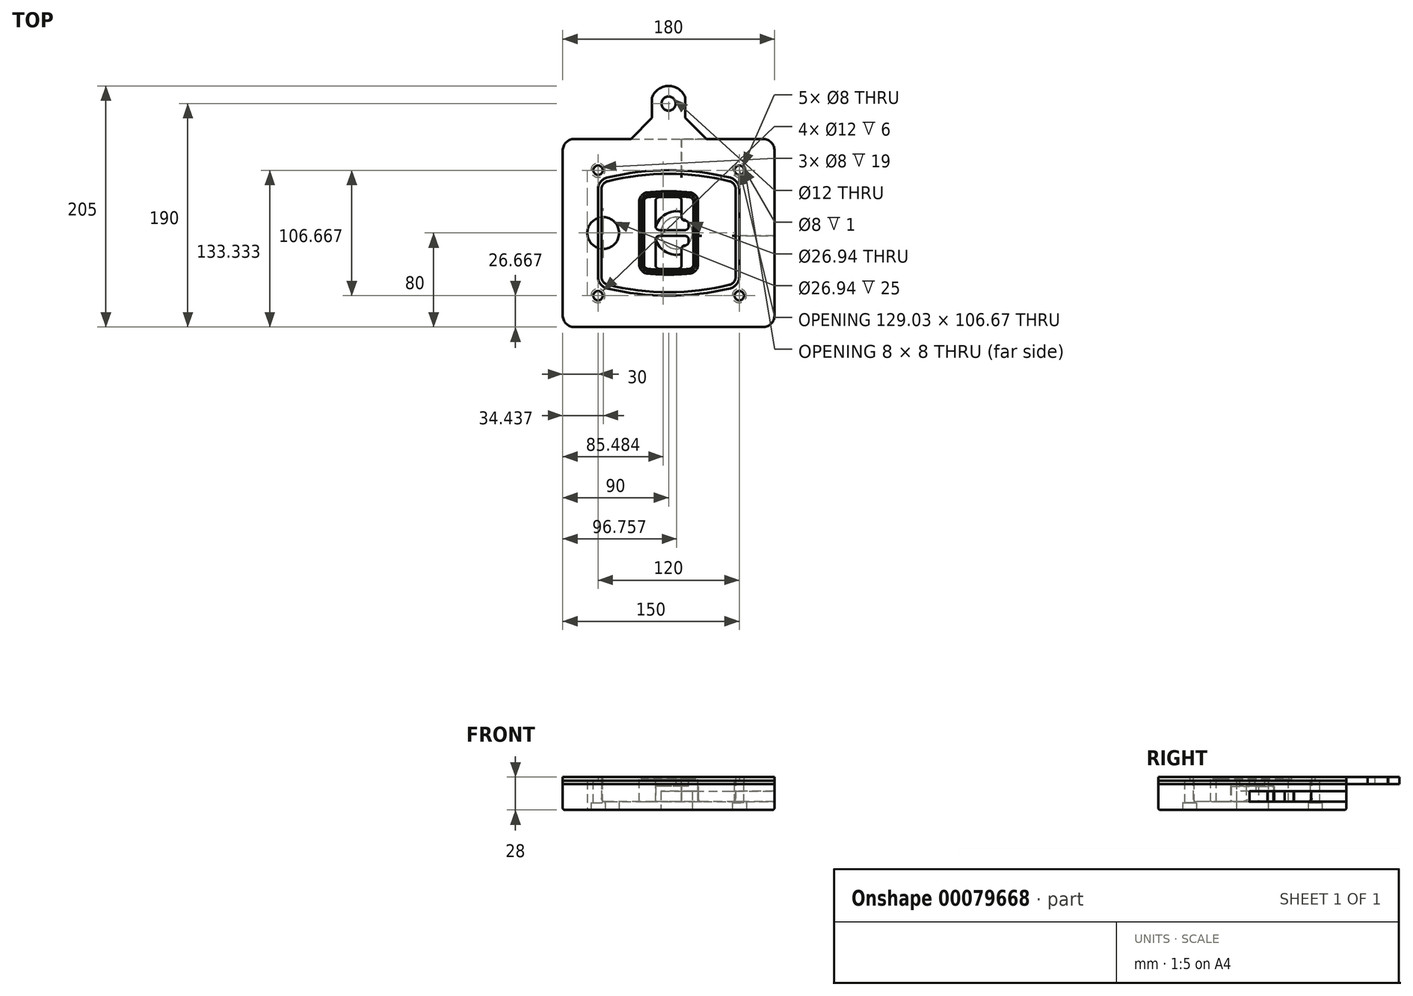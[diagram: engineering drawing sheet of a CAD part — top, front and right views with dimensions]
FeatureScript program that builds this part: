
annotation { "Feature Type Name" : "Feature", "Feature Type Description" : "" }
export const myFeature = defineFeature(function(context is Context, id is Id, definition is map)
    precondition{}
    {
        {
            var Q0;
            Q0=qCreatedBy(makeId("Top.planeOp"),FACE);
            var sketch = newSketch(context, id + "F0", { "sketchPlane" : qUnion([Q0])});
            skPoint(sketch, "E0.rect.middle", {"position": v(0, 0) * mm});
            skLineSegment(sketch, "E1.bottom", {"start": v(-80, -80) * mm, "end": v(80, -80) * mm});
            skLineSegment(sketch, "E1.top", {"start": v(-80, 80) * mm, "end": v(80, 80) * mm});
            skLineSegment(sketch, "E1.left", {"start": v(-90, -70) * mm, "end": v(-90, 70) * mm});
            skLineSegment(sketch, "E1.right", {"start": v(90, -70) * mm, "end": v(90, 70) * mm});
            skLineSegment(sketch, "E2", {"start": v(-90, 80) * mm, "end": v(90, -80) * mm, "construction": true});
            skLineSegment(sketch, "E3", {"start": v(90, 80) * mm, "end": v(-90, -80) * mm, "construction": true});
            skCircle(sketch, "E4", {"center": v(-60, 53.33) * mm, "radius": 4 * mm});
            skCircle(sketch, "E5", {"center": v(60, 53.33) * mm, "radius": 4 * mm});
            skCircle(sketch, "E6", {"center": v(60, -53.33) * mm, "radius": 4 * mm});
            skCircle(sketch, "E7", {"center": v(-60, -53.33) * mm, "radius": 4 * mm});
            skLineSegment(sketch, "E8", {"start": v(-60, 53.33) * mm, "end": v(60, 53.33) * mm, "construction": true});
            skLineSegment(sketch, "E9", {"start": v(60, 53.33) * mm, "end": v(60, -53.33) * mm, "construction": true});
            skLineSegment(sketch, "E10", {"start": v(60, -53.33) * mm, "end": v(-60, -53.33) * mm, "construction": true});
            skLineSegment(sketch, "E11", {"start": v(-60, -53.33) * mm, "end": v(-60, 53.33) * mm, "construction": true});
            skLineSegment(sketch, "E12", {"start": v(-60, 37.3) * mm, "end": v(-60, -37.3) * mm});
            skLineSegment(sketch, "E13", {"start": v(60, 37.3) * mm, "end": v(60, -37.3) * mm});
            skArc(sketch, "E14", {"start": v(52.38, 47.01) * mm, "mid": v(0, 53.33) * mm, "end": v(-52.38, 47.01) * mm});
            skArc(sketch, "E15", {"start": v(-52.38, -47.01) * mm, "mid": v(0, -53.33) * mm, "end": v(52.38, -47.01) * mm});
            skLineSegment(sketch, "E16", {"start": v(-60, 0) * mm, "end": v(60, 0) * mm, "construction": true});
            skPoint(sketch, "E17.visualSharp", {"position": v(-60, -45) * mm});
            skArc(sketch, "E17.filletArc", {"start": v(-60, -37.3) * mm, "mid": v(-57.87, -43.47) * mm, "end": v(-52.38, -47.01) * mm});
            skPoint(sketch, "E18.visualSharp", {"position": v(-60, 45) * mm});
            skArc(sketch, "E18.filletArc", {"start": v(-52.38, 47.01) * mm, "mid": v(-57.87, 43.47) * mm, "end": v(-60, 37.3) * mm});
            skPoint(sketch, "E19.visualSharp", {"position": v(60, 45) * mm});
            skArc(sketch, "E19.filletArc", {"start": v(60, 37.3) * mm, "mid": v(57.87, 43.47) * mm, "end": v(52.38, 47.01) * mm});
            skPoint(sketch, "E20.visualSharp", {"position": v(60, -45) * mm});
            skArc(sketch, "E20.filletArc", {"start": v(52.38, -47.01) * mm, "mid": v(57.87, -43.47) * mm, "end": v(60, -37.3) * mm});
            skPoint(sketch, "E21.visualSharp", {"position": v(-90, 80) * mm});
            skArc(sketch, "E21.filletArc", {"start": v(-80, 80) * mm, "mid": v(-87.07, 77.07) * mm, "end": v(-90, 70) * mm});
            skPoint(sketch, "E22.visualSharp", {"position": v(90, 80) * mm});
            skArc(sketch, "E22.filletArc", {"start": v(90, 70) * mm, "mid": v(87.07, 77.07) * mm, "end": v(80, 80) * mm});
            skPoint(sketch, "E23.visualSharp", {"position": v(90, -80) * mm});
            skArc(sketch, "E23.filletArc", {"start": v(80, -80) * mm, "mid": v(87.07, -77.07) * mm, "end": v(90, -70) * mm});
            skPoint(sketch, "E24.visualSharp", {"position": v(-90, -80) * mm});
            skArc(sketch, "E24.filletArc", {"start": v(-90, -70) * mm, "mid": v(-87.07, -77.07) * mm, "end": v(-80, -80) * mm});
            skArc(sketch, "E25.0", {"start": v(57, 37.3) * mm, "mid": v(55.5, 41.62) * mm, "end": v(51.67, 44.1) * mm});
            skLineSegment(sketch, "E25.1", {"start": v(57, 37.3) * mm, "end": v(57, -37.3) * mm});
            skArc(sketch, "E25.2", {"start": v(51.67, -44.1) * mm, "mid": v(55.5, -41.62) * mm, "end": v(57, -37.3) * mm});
            skArc(sketch, "E25.3", {"start": v(-51.67, -44.1) * mm, "mid": v(0, -50.33) * mm, "end": v(51.67, -44.1) * mm});
            skArc(sketch, "E25.4", {"start": v(-57, -37.3) * mm, "mid": v(-55.5, -41.62) * mm, "end": v(-51.67, -44.1) * mm});
            skArc(sketch, "E25.5", {"start": v(51.67, 44.1) * mm, "mid": v(0, 50.33) * mm, "end": v(-51.67, 44.1) * mm});
            skLineSegment(sketch, "E25.6", {"start": v(-57, 37.3) * mm, "end": v(-57, -37.3) * mm});
            skArc(sketch, "E25.7", {"start": v(-51.67, 44.1) * mm, "mid": v(-55.5, 41.62) * mm, "end": v(-57, 37.3) * mm});
            skArc(sketch, "E26.0", {"start": v(-53.33, 50.9) * mm, "mid": v(-61.01, 45.94) * mm, "end": v(-64, 37.3) * mm});
            skArc(sketch, "E26.1", {"start": v(53.33, 50.9) * mm, "mid": v(0, 57.33) * mm, "end": v(-53.33, 50.9) * mm});
            skArc(sketch, "E26.2", {"start": v(64, 37.3) * mm, "mid": v(61.01, 45.94) * mm, "end": v(53.33, 50.9) * mm});
            skLineSegment(sketch, "E26.3", {"start": v(64, 37.3) * mm, "end": v(64, -37.3) * mm});
            skArc(sketch, "E26.4", {"start": v(53.33, -50.9) * mm, "mid": v(61.01, -45.94) * mm, "end": v(64, -37.3) * mm});
            skLineSegment(sketch, "E26.5", {"start": v(-64, 37.3) * mm, "end": v(-64, -37.3) * mm});
            skArc(sketch, "E26.6", {"start": v(-53.33, -50.9) * mm, "mid": v(0, -57.33) * mm, "end": v(53.33, -50.9) * mm});
            skArc(sketch, "E26.7", {"start": v(-64, -37.3) * mm, "mid": v(-61.01, -45.94) * mm, "end": v(-53.33, -50.9) * mm});
            skSolve(sketch);
        }
        {
            var Q0;
            Q0=makeQuery(id+"F0.imprint","IMPRINT",FACE,{"disambiguationData":[TD([[makeQuery(id+"F0.imprint","IMPRINT",EDGE,{"derivedFrom":sQuery(id+"F0.wireOp",EDGE,"E1.bottom")}),1.0]])]});
            var Q1;
            Q1=makeQuery(id+"F0.imprint","IMPRINT",FACE,{"disambiguationData":[TD([[makeQuery(id+"F0.imprint","IMPRINT",EDGE,{"derivedFrom":sQuery(id+"F0.wireOp",EDGE,"E12")}),1.0]])]});
            var Q2;
            Q2=makeQuery(id+"F0.imprint","IMPRINT",FACE,{"disambiguationData":[TD([[makeQuery(id+"F0.imprint","IMPRINT",EDGE,{"derivedFrom":sQuery(id+"F0.wireOp",EDGE,"E25.0")}),1.0]])]});
            var Q3;
            Q3=makeQuery(id+"F0.imprint","IMPRINT",FACE,{"disambiguationData":[TD([[makeQuery(id+"F0.imprint","IMPRINT",EDGE,{"derivedFrom":sQuery(id+"F0.wireOp",EDGE,"E12")}),-1.0]])]});
            extrude(context, id + "F1", {"entities" : qUnion([Q0, Q1, Q2, Q3]), "oppositeDirection" : true, "depth" : 25 * mm});
        }
        {
            var Q0;
            Q0=makeQuery(id+"F0.imprint","IMPRINT",FACE,{"disambiguationData":[TD([[makeQuery(id+"F0.imprint","IMPRINT",EDGE,{"derivedFrom":sQuery(id+"F0.wireOp",EDGE,"E12")}),1.0]])]});
            extrude(context, id + "F2", {"entities" : qUnion([Q0]), "operationType" : NewBodyOperationType.ADD, "depth" : 3 * mm});
        }
        {
            var Q0;
            Q0=makeQuery(id+"F0.imprint","IMPRINT",FACE,{"disambiguationData":[TD([[makeQuery(id+"F0.imprint","IMPRINT",EDGE,{"derivedFrom":sQuery(id+"F0.wireOp",EDGE,"E25.0")}),1.0]])]});
            extrude(context, id + "F3", {"entities" : qUnion([Q0]), "operationType" : NewBodyOperationType.REMOVE, "oppositeDirection" : true, "depth" : 18 * mm});
        }
        {
            var Q0;
            Q0=makeQuery(id+"F2.opExtrude","CAP_FACE",FACE,{"disambiguationData":[OSD([sQuery(id+"F0.wireOp",EDGE,"E12"),sQuery(id+"F0.wireOp",EDGE,"E13"),sQuery(id+"F0.wireOp",EDGE,"E14"),sQuery(id+"F0.wireOp",EDGE,"E15"),sQuery(id+"F0.wireOp",EDGE,"E17.filletArc"),sQuery(id+"F0.wireOp",EDGE,"E18.filletArc"),sQuery(id+"F0.wireOp",EDGE,"E19.filletArc"),sQuery(id+"F0.wireOp",EDGE,"E20.filletArc"),sQuery(id+"F0.wireOp",EDGE,"E25.0"),sQuery(id+"F0.wireOp",EDGE,"E25.1"),sQuery(id+"F0.wireOp",EDGE,"E25.2"),sQuery(id+"F0.wireOp",EDGE,"E25.3"),sQuery(id+"F0.wireOp",EDGE,"E25.4"),sQuery(id+"F0.wireOp",EDGE,"E25.5"),sQuery(id+"F0.wireOp",EDGE,"E25.6"),sQuery(id+"F0.wireOp",EDGE,"E25.7")])],"isStart":false});
            var sketch = newSketch(context, id + "F4", { "sketchPlane" : qUnion([Q0])});
            skArc(sketch, "E27.0", {"start": v(-17.7, -34.56) * mm, "mid": v(0, -35.33) * mm, "end": v(17.7, -34.56) * mm});
            skArc(sketch, "E28.0", {"start": v(17.7, 34.56) * mm, "mid": v(0, 35.33) * mm, "end": v(-17.7, 34.56) * mm});
            skLineSegment(sketch, "E29", {"start": v(-25, 26.59) * mm, "end": v(-25, -26.59) * mm});
            skLineSegment(sketch, "E30", {"start": v(25, 26.59) * mm, "end": v(25, -26.59) * mm});
            skLineSegment(sketch, "E31", {"start": v(-25, 33.78) * mm, "end": v(25, 33.78) * mm, "construction": true});
            skLineSegment(sketch, "E32", {"start": v(-25, -33.78) * mm, "end": v(25, -33.78) * mm, "construction": true});
            skPoint(sketch, "E33.visualSharp", {"position": v(-25, 33.78) * mm});
            skArc(sketch, "E33.filletArc", {"start": v(-17.7, 34.56) * mm, "mid": v(-22.9, 32) * mm, "end": v(-25, 26.59) * mm});
            skPoint(sketch, "E34.visualSharp", {"position": v(25, 33.78) * mm});
            skArc(sketch, "E34.filletArc", {"start": v(25, 26.59) * mm, "mid": v(22.9, 32) * mm, "end": v(17.7, 34.56) * mm});
            skPoint(sketch, "E35.visualSharp", {"position": v(25, -33.78) * mm});
            skArc(sketch, "E35.filletArc", {"start": v(17.7, -34.56) * mm, "mid": v(22.9, -32) * mm, "end": v(25, -26.59) * mm});
            skPoint(sketch, "E36.visualSharp", {"position": v(-25, -33.78) * mm});
            skArc(sketch, "E36.filletArc", {"start": v(-25, -26.59) * mm, "mid": v(-22.9, -32) * mm, "end": v(-17.7, -34.56) * mm});
            skArc(sketch, "E37.0", {"start": v(51.67, 44.1) * mm, "mid": v(0, 50.33) * mm, "end": v(-51.67, 44.1) * mm});
            skArc(sketch, "E37.1", {"start": v(-51.67, 44.1) * mm, "mid": v(-55.5, 41.62) * mm, "end": v(-57, 37.3) * mm});
            skLineSegment(sketch, "E37.2", {"start": v(-57, 37.3) * mm, "end": v(-57, -37.3) * mm});
            skArc(sketch, "E37.3", {"start": v(-57, -37.3) * mm, "mid": v(-55.5, -41.62) * mm, "end": v(-51.67, -44.1) * mm});
            skArc(sketch, "E37.4", {"start": v(-51.67, -44.1) * mm, "mid": v(0, -50.33) * mm, "end": v(51.67, -44.1) * mm});
            skArc(sketch, "E37.5", {"start": v(51.67, -44.1) * mm, "mid": v(55.5, -41.62) * mm, "end": v(57, -37.3) * mm});
            skLineSegment(sketch, "E37.6", {"start": v(57, 37.3) * mm, "end": v(57, -37.3) * mm});
            skArc(sketch, "E37.7", {"start": v(57, 37.3) * mm, "mid": v(55.5, 41.62) * mm, "end": v(51.67, 44.1) * mm});
            skLineSegment(sketch, "E38.0", {"start": v(23, 26.59) * mm, "end": v(23, -26.59) * mm});
            skArc(sketch, "E38.1", {"start": v(17.53, -32.56) * mm, "mid": v(21.42, -30.64) * mm, "end": v(23, -26.59) * mm});
            skArc(sketch, "E38.2", {"start": v(-17.53, -32.56) * mm, "mid": v(0, -33.33) * mm, "end": v(17.53, -32.56) * mm});
            skArc(sketch, "E38.3", {"start": v(-23, -26.59) * mm, "mid": v(-21.42, -30.64) * mm, "end": v(-17.53, -32.56) * mm});
            skLineSegment(sketch, "E38.4", {"start": v(-23, 26.59) * mm, "end": v(-23, -26.59) * mm});
            skArc(sketch, "E38.5", {"start": v(23, 26.59) * mm, "mid": v(21.42, 30.64) * mm, "end": v(17.53, 32.56) * mm});
            skArc(sketch, "E38.6", {"start": v(-17.53, 32.56) * mm, "mid": v(-21.42, 30.64) * mm, "end": v(-23, 26.59) * mm});
            skArc(sketch, "E38.7", {"start": v(17.53, 32.56) * mm, "mid": v(0, 33.33) * mm, "end": v(-17.53, 32.56) * mm});
            skArc(sketch, "E39.0", {"start": v(21, 26.59) * mm, "mid": v(19.95, 29.29) * mm, "end": v(17.35, 30.57) * mm});
            skLineSegment(sketch, "E39.1", {"start": v(21, 26.59) * mm, "end": v(21, -26.59) * mm});
            skArc(sketch, "E39.2", {"start": v(17.35, -30.57) * mm, "mid": v(19.95, -29.29) * mm, "end": v(21, -26.59) * mm});
            skArc(sketch, "E39.3", {"start": v(-17.35, -30.57) * mm, "mid": v(0, -31.33) * mm, "end": v(17.35, -30.57) * mm});
            skArc(sketch, "E39.4", {"start": v(-21, -26.59) * mm, "mid": v(-19.95, -29.29) * mm, "end": v(-17.35, -30.57) * mm});
            skArc(sketch, "E39.5", {"start": v(17.35, 30.57) * mm, "mid": v(0, 31.33) * mm, "end": v(-17.35, 30.57) * mm});
            skLineSegment(sketch, "E39.6", {"start": v(-21, 26.59) * mm, "end": v(-21, -26.59) * mm});
            skArc(sketch, "E39.7", {"start": v(-17.35, 30.57) * mm, "mid": v(-19.95, 29.29) * mm, "end": v(-21, 26.59) * mm});
            skLineSegment(sketch, "E40", {"start": v(-25, 0) * mm, "end": v(25, 0) * mm, "construction": true});
            skLineSegment(sketch, "E41", {"start": v(-11, 5.5) * mm, "end": v(-11, 27.5) * mm});
            skLineSegment(sketch, "E42", {"start": v(-8, 30.5) * mm, "end": v(8, 30.5) * mm});
            skLineSegment(sketch, "E43", {"start": v(11, 27.5) * mm, "end": v(11, 13.5) * mm});
            skLineSegment(sketch, "E44", {"start": v(14, 10.5) * mm, "end": v(14, 10.5) * mm});
            skLineSegment(sketch, "E45", {"start": v(17, 7.5) * mm, "end": v(17, 5.5) * mm});
            skLineSegment(sketch, "E46", {"start": v(14, 2.5) * mm, "end": v(-8, 2.5) * mm});
            skPoint(sketch, "E47.visualSharp", {"position": v(-11, 30.5) * mm});
            skArc(sketch, "E47.filletArc", {"start": v(-8, 30.5) * mm, "mid": v(-10.12, 29.62) * mm, "end": v(-11, 27.5) * mm});
            skPoint(sketch, "E48.visualSharp", {"position": v(11, 30.5) * mm});
            skArc(sketch, "E48.filletArc", {"start": v(11, 27.5) * mm, "mid": v(10.12, 29.62) * mm, "end": v(8, 30.5) * mm});
            skPoint(sketch, "E49.visualSharp", {"position": v(11, 10.5) * mm});
            skArc(sketch, "E49.filletArc", {"start": v(11, 13.5) * mm, "mid": v(11.88, 11.38) * mm, "end": v(14, 10.5) * mm});
            skPoint(sketch, "E50.visualSharp", {"position": v(17, 10.5) * mm});
            skArc(sketch, "E50.filletArc", {"start": v(17, 7.5) * mm, "mid": v(16.12, 9.62) * mm, "end": v(14, 10.5) * mm});
            skPoint(sketch, "E51.visualSharp", {"position": v(17, 2.5) * mm});
            skArc(sketch, "E51.filletArc", {"start": v(14, 2.5) * mm, "mid": v(16.12, 3.38) * mm, "end": v(17, 5.5) * mm});
            skPoint(sketch, "E52.visualSharp", {"position": v(-11, 2.5) * mm});
            skArc(sketch, "E52.filletArc", {"start": v(-11, 5.5) * mm, "mid": v(-10.12, 3.38) * mm, "end": v(-8, 2.5) * mm});
            skLineSegment(sketch, "E53.0.MirrorCS", {"start": v(14, -2.5) * mm, "end": v(-8, -2.5) * mm});
            skArc(sketch, "E54.0.MirrorCS", {"start": v(-11, -5.5) * mm, "mid": v(-10.12, -3.38) * mm, "end": v(-8, -2.5) * mm});
            skLineSegment(sketch, "E55.0.MirrorCS", {"start": v(-11, -5.5) * mm, "end": v(-11, -27.5) * mm});
            skArc(sketch, "E56.0.MirrorCS", {"start": v(-8, -30.5) * mm, "mid": v(-10.12, -29.62) * mm, "end": v(-11, -27.5) * mm});
            skLineSegment(sketch, "E57.0.MirrorCS", {"start": v(-8, -30.5) * mm, "end": v(8, -30.5) * mm});
            skArc(sketch, "E58.0.MirrorCS", {"start": v(11, -27.5) * mm, "mid": v(10.12, -29.62) * mm, "end": v(8, -30.5) * mm});
            skLineSegment(sketch, "E59.0.MirrorCS", {"start": v(11, -27.5) * mm, "end": v(11, -13.5) * mm});
            skArc(sketch, "E60.0.MirrorCS", {"start": v(11, -13.5) * mm, "mid": v(11.88, -11.38) * mm, "end": v(14, -10.5) * mm});
            skArc(sketch, "E61.0.MirrorCS", {"start": v(17, -7.5) * mm, "mid": v(16.12, -9.62) * mm, "end": v(14, -10.5) * mm});
            skLineSegment(sketch, "E62.0.MirrorCS", {"start": v(17, -7.5) * mm, "end": v(17, -5.5) * mm});
            skArc(sketch, "E63.0.MirrorCS", {"start": v(14, -2.5) * mm, "mid": v(16.12, -3.38) * mm, "end": v(17, -5.5) * mm});
            skSolve(sketch);
        }
        {
            var Q0;
            Q0=makeQuery(id+"F4.imprint","IMPRINT",FACE,{"disambiguationData":[TD([[makeQuery(id+"F4.imprint","IMPRINT",EDGE,{"derivedFrom":sQuery(id+"F4.wireOp",EDGE,"E27.0")}),1.0]])]});
            var Q1;
            Q1=makeQuery(id+"F4.imprint","IMPRINT",FACE,{"disambiguationData":[TD([[makeQuery(id+"F4.imprint","IMPRINT",EDGE,{"derivedFrom":sQuery(id+"F4.wireOp",EDGE,"E38.0")}),-1.0]])]});
            var Q2;
            Q2=makeQuery(id+"F4.imprint","IMPRINT",FACE,{"disambiguationData":[TD([[makeQuery(id+"F4.imprint","IMPRINT",EDGE,{"derivedFrom":sQuery(id+"F4.wireOp",EDGE,"E39.0")}),1.0]])]});
            extrude(context, id + "F5", {"entities" : qUnion([Q0, Q1, Q2]), "operationType" : NewBodyOperationType.ADD, "endBound" : BoundingType.UP_TO_NEXT, "oppositeDirection" : true, "depth" : 25 * mm});
        }
        {
            var Q0;
            Q0=makeQuery(id+"F4.imprint","IMPRINT",FACE,{"disambiguationData":[TD([[makeQuery(id+"F4.imprint","IMPRINT",EDGE,{"derivedFrom":sQuery(id+"F4.wireOp",EDGE,"E38.0")}),-1.0]])]});
            extrude(context, id + "F6", {"entities" : qUnion([Q0]), "operationType" : NewBodyOperationType.REMOVE, "oppositeDirection" : true, "depth" : 2 * mm});
        }
        {
            var Q0;
            Q0=makeQuery(id+"F1.opExtrude","CAP_FACE",FACE,{"disambiguationData":[OSD([sQuery(id+"F0.wireOp",EDGE,"E1.bottom"),sQuery(id+"F0.wireOp",EDGE,"E1.top"),sQuery(id+"F0.wireOp",EDGE,"E1.left"),sQuery(id+"F0.wireOp",EDGE,"E1.right"),sQuery(id+"F0.wireOp",EDGE,"E4"),sQuery(id+"F0.wireOp",EDGE,"E5"),sQuery(id+"F0.wireOp",EDGE,"E6"),sQuery(id+"F0.wireOp",EDGE,"E7"),sQuery(id+"F0.wireOp",EDGE,"E21.filletArc"),sQuery(id+"F0.wireOp",EDGE,"E22.filletArc"),sQuery(id+"F0.wireOp",EDGE,"E23.filletArc"),sQuery(id+"F0.wireOp",EDGE,"E24.filletArc")])],"isStart":false});
            var sketch = newSketch(context, id + "F7", { "sketchPlane" : qUnion([Q0])});
            skCircle(sketch, "E64", {"center": v(6.76, 0) * mm, "radius": 13.47 * mm});
            skCircle(sketch, "E65", {"center": v(-55.56, 0) * mm, "radius": 13.47 * mm});
            skLineSegment(sketch, "E66", {"start": v(90, 0) * mm, "end": v(-90, 0) * mm});
            skCircle(sketch, "E67", {"center": v(6.76, 0) * mm, "radius": 18.47 * mm});
            skCircle(sketch, "E68", {"center": v(60, -53.33) * mm, "radius": 6 * mm});
            skCircle(sketch, "E69", {"center": v(-60, -53.33) * mm, "radius": 6 * mm});
            skCircle(sketch, "E70", {"center": v(-60, 53.33) * mm, "radius": 6 * mm});
            skCircle(sketch, "E71", {"center": v(60, 53.33) * mm, "radius": 6 * mm});
            skSolve(sketch);
        }
        {
            var Q0;
            {var subQ1=sQuery(id+"F7.wireOp",EDGE,"E66");var subQ4=sQuery(id+"F7.wireOp",EDGE,"E64");var subQ6=makeQuery(id+"F7.imprint","INTERSECT",VERTEX,{"disambiguationData":[OD(0.0)],"derivedFrom":[subQ4,subQ1]});Q0=makeQuery(id+"F7.imprint","IMPRINT",FACE,{"disambiguationData":[TD([[makeQuery(id+"F7.imprint","IMPRINT",EDGE,{"disambiguationData":[TD([[subQ6,-1.0]])],"derivedFrom":subQ4}),-1.0]])]});}
            var Q1;
            {var subQ0=sQuery(id+"F7.wireOp",EDGE,"E66");var subQ1=sQuery(id+"F7.wireOp",EDGE,"E64");var subQ3=makeQuery(id+"F7.imprint","INTERSECT",VERTEX,{"disambiguationData":[OD(0.0)],"derivedFrom":[subQ1,subQ0]});Q1=makeQuery(id+"F7.imprint","IMPRINT",FACE,{"disambiguationData":[TD([[makeQuery(id+"F7.imprint","IMPRINT",EDGE,{"disambiguationData":[TD([[subQ3,-1.0]])],"derivedFrom":subQ1}),1.0]])]});}
            var Q2;
            {var subQ0=sQuery(id+"F7.wireOp",EDGE,"E66");var subQ1=sQuery(id+"F7.wireOp",EDGE,"E64");var subQ3=makeQuery(id+"F7.imprint","INTERSECT",VERTEX,{"disambiguationData":[OD(0.0)],"derivedFrom":[subQ1,subQ0]});Q2=makeQuery(id+"F7.imprint","IMPRINT",FACE,{"disambiguationData":[TD([[makeQuery(id+"F7.imprint","IMPRINT",EDGE,{"disambiguationData":[TD([[subQ3,1.0]])],"derivedFrom":subQ1}),1.0]])]});}
            var Q3;
            {var subQ1=sQuery(id+"F7.wireOp",EDGE,"E66");var subQ4=sQuery(id+"F7.wireOp",EDGE,"E64");var subQ6=makeQuery(id+"F7.imprint","INTERSECT",VERTEX,{"disambiguationData":[OD(0.0)],"derivedFrom":[subQ4,subQ1]});Q3=makeQuery(id+"F7.imprint","IMPRINT",FACE,{"disambiguationData":[TD([[makeQuery(id+"F7.imprint","IMPRINT",EDGE,{"disambiguationData":[TD([[subQ6,1.0]])],"derivedFrom":subQ4}),-1.0]])]});}
            extrude(context, id + "F8", {"entities" : qUnion([Q0, Q1, Q2, Q3]), "operationType" : NewBodyOperationType.ADD, "oppositeDirection" : true, "depth" : 20 * mm});
        }
        {
            var Q0;
            {var subQ0=sQuery(id+"F7.wireOp",EDGE,"E66");var subQ1=sQuery(id+"F7.wireOp",EDGE,"E64");var subQ3=makeQuery(id+"F7.imprint","INTERSECT",VERTEX,{"disambiguationData":[OD(0.0)],"derivedFrom":[subQ1,subQ0]});Q0=makeQuery(id+"F7.imprint","IMPRINT",FACE,{"disambiguationData":[TD([[makeQuery(id+"F7.imprint","IMPRINT",EDGE,{"disambiguationData":[TD([[subQ3,-1.0]])],"derivedFrom":subQ1}),1.0]])]});}
            var Q1;
            {var subQ0=sQuery(id+"F7.wireOp",EDGE,"E66");var subQ1=sQuery(id+"F7.wireOp",EDGE,"E64");var subQ3=makeQuery(id+"F7.imprint","INTERSECT",VERTEX,{"disambiguationData":[OD(0.0)],"derivedFrom":[subQ1,subQ0]});Q1=makeQuery(id+"F7.imprint","IMPRINT",FACE,{"disambiguationData":[TD([[makeQuery(id+"F7.imprint","IMPRINT",EDGE,{"disambiguationData":[TD([[subQ3,1.0]])],"derivedFrom":subQ1}),1.0]])]});}
            extrude(context, id + "F9", {"entities" : qUnion([Q0, Q1]), "operationType" : NewBodyOperationType.REMOVE, "oppositeDirection" : true, "depth" : 16 * mm});
        }
        {
            var Q0;
            {var subQ0=sQuery(id+"F7.wireOp",EDGE,"E66");var subQ1=sQuery(id+"F7.wireOp",EDGE,"E65");var subQ3=makeQuery(id+"F7.imprint","INTERSECT",VERTEX,{"disambiguationData":[OD(0.0)],"derivedFrom":[subQ1,subQ0]});Q0=makeQuery(id+"F7.imprint","IMPRINT",FACE,{"disambiguationData":[TD([[makeQuery(id+"F7.imprint","IMPRINT",EDGE,{"disambiguationData":[TD([[subQ3,-1.0]])],"derivedFrom":subQ1}),1.0]])]});}
            var Q1;
            {var subQ0=sQuery(id+"F7.wireOp",EDGE,"E66");var subQ1=sQuery(id+"F7.wireOp",EDGE,"E65");var subQ3=makeQuery(id+"F7.imprint","INTERSECT",VERTEX,{"disambiguationData":[OD(0.0)],"derivedFrom":[subQ1,subQ0]});Q1=makeQuery(id+"F7.imprint","IMPRINT",FACE,{"disambiguationData":[TD([[makeQuery(id+"F7.imprint","IMPRINT",EDGE,{"disambiguationData":[TD([[subQ3,1.0]])],"derivedFrom":subQ1}),1.0]])]});}
            extrude(context, id + "F10", {"entities" : qUnion([Q0, Q1]), "operationType" : NewBodyOperationType.REMOVE, "oppositeDirection" : true, "depth" : 25 * mm});
        }
        {
            var Q0;
            Q0=makeQuery(id+"F7.imprint","IMPRINT",FACE,{"disambiguationData":[TD([[makeQuery(id+"F7.imprint","IMPRINT",EDGE,{"derivedFrom":sQuery(id+"F7.wireOp",EDGE,"E68")}),1.0]])]});
            var Q1;
            Q1=makeQuery(id+"F7.imprint","IMPRINT",FACE,{"disambiguationData":[TD([[makeQuery(id+"F7.imprint","IMPRINT",EDGE,{"derivedFrom":makeQuery(id+"F1.opExtrude","CAP_EDGE",EDGE,{"disambiguationData":[OSD([sQuery(id+"F0.wireOp",EDGE,"E5")])],"isStart":false})}),-1.0]])]});
            var Q2;
            Q2=makeQuery(id+"F7.imprint","IMPRINT",FACE,{"disambiguationData":[TD([[makeQuery(id+"F7.imprint","IMPRINT",EDGE,{"derivedFrom":sQuery(id+"F7.wireOp",EDGE,"E69")}),1.0]])]});
            var Q3;
            Q3=makeQuery(id+"F7.imprint","IMPRINT",FACE,{"disambiguationData":[TD([[makeQuery(id+"F7.imprint","IMPRINT",EDGE,{"derivedFrom":makeQuery(id+"F1.opExtrude","CAP_EDGE",EDGE,{"disambiguationData":[OSD([sQuery(id+"F0.wireOp",EDGE,"E4")])],"isStart":false})}),-1.0]])]});
            var Q4;
            Q4=makeQuery(id+"F7.imprint","IMPRINT",FACE,{"disambiguationData":[TD([[makeQuery(id+"F7.imprint","IMPRINT",EDGE,{"derivedFrom":sQuery(id+"F7.wireOp",EDGE,"E70")}),1.0]])]});
            var Q5;
            Q5=makeQuery(id+"F7.imprint","IMPRINT",FACE,{"disambiguationData":[TD([[makeQuery(id+"F7.imprint","IMPRINT",EDGE,{"derivedFrom":makeQuery(id+"F1.opExtrude","CAP_EDGE",EDGE,{"disambiguationData":[OSD([sQuery(id+"F0.wireOp",EDGE,"E7")])],"isStart":false})}),-1.0]])]});
            var Q6;
            Q6=makeQuery(id+"F7.imprint","IMPRINT",FACE,{"disambiguationData":[TD([[makeQuery(id+"F7.imprint","IMPRINT",EDGE,{"derivedFrom":sQuery(id+"F7.wireOp",EDGE,"E71")}),1.0]])]});
            var Q7;
            Q7=makeQuery(id+"F7.imprint","IMPRINT",FACE,{"disambiguationData":[TD([[makeQuery(id+"F7.imprint","IMPRINT",EDGE,{"derivedFrom":makeQuery(id+"F1.opExtrude","CAP_EDGE",EDGE,{"disambiguationData":[OSD([sQuery(id+"F0.wireOp",EDGE,"E6")])],"isStart":false})}),-1.0]])]});
            extrude(context, id + "F11", {"entities" : qUnion([Q0, Q1, Q2, Q3, Q4, Q5, Q6, Q7]), "operationType" : NewBodyOperationType.REMOVE, "oppositeDirection" : true, "depth" : 6 * mm});
        }
        {
            var Q0;
            Q0=makeQuery(id+"F9.boolean.opBoolean","COPY",FACE,{"derivedFrom":makeQuery(id+"F9.opExtrude","CAP_FACE",FACE,{"disambiguationData":[OSD([sQuery(id+"F7.wireOp",EDGE,"E64")])],"isStart":false})});
            var sketch = newSketch(context, id + "F12", { "sketchPlane" : qUnion([Q0])});
            skArc(sketch, "E72.0", {"start": v(11, -88.19) * mm, "mid": v(97.1, -83.6) * mm, "end": v(92.5, 2.5) * mm});
            skLineSegment(sketch, "E72.1", {"start": v(11, -17.97) * mm, "end": v(11, -17.97) * mm});
            skLineSegment(sketch, "E73", {"start": v(92.5, -105.13) * mm, "end": v(102.3, -105.13) * mm});
            skLineSegment(sketch, "E74.0", {"start": v(92.5, 2.5) * mm, "end": v(14, 2.5) * mm});
            skArc(sketch, "E74.1", {"start": v(14, 2.5) * mm, "mid": v(16.12, 3.38) * mm, "end": v(17, 5.5) * mm});
            skLineSegment(sketch, "E74.2", {"start": v(17, 7.5) * mm, "end": v(17, 5.5) * mm});
            skArc(sketch, "E74.3", {"start": v(17, 7.5) * mm, "mid": v(16.12, 9.62) * mm, "end": v(14, 10.5) * mm});
            skArc(sketch, "E74.4", {"start": v(11, 13.5) * mm, "mid": v(11.88, 11.38) * mm, "end": v(14, 10.5) * mm});
            skLineSegment(sketch, "E74.5", {"start": v(11, 13.5) * mm, "end": v(11, -88.19) * mm});
            skLineSegment(sketch, "E74.7", {"start": v(92.5, -2.5) * mm, "end": v(14, -2.5) * mm});
            skArc(sketch, "E74.8", {"start": v(14, -2.5) * mm, "mid": v(16.12, -3.38) * mm, "end": v(17, -5.5) * mm});
            skLineSegment(sketch, "E74.9", {"start": v(17, -7.5) * mm, "end": v(17, -5.5) * mm});
            skArc(sketch, "E74.10", {"start": v(17, -7.5) * mm, "mid": v(16.12, -9.62) * mm, "end": v(14, -10.5) * mm});
            skArc(sketch, "E74.11", {"start": v(11, -13.5) * mm, "mid": v(11.88, -11.38) * mm, "end": v(14, -10.5) * mm});
            skLineSegment(sketch, "E74.12", {"start": v(11, -17.97) * mm, "end": v(11, -13.5) * mm});
            skPoint(sketch, "E75.orphan", {"position": v(11, -27.5) * mm});
            skPoint(sketch, "E76.orphan", {"position": v(-8, -2.5) * mm});
            skPoint(sketch, "E77.orphan", {"position": v(-8, 2.5) * mm});
            skPoint(sketch, "E78.orphan", {"position": v(11, 27.5) * mm});
            skSolve(sketch);
        }
        {
            var Q0;
            {var subQ7=sQuery(id+"F12.wireOp",EDGE,"E72.0");var subQ14=sQuery(id+"F12.wireOp",EDGE,"E72.1");var subQ16=sQuery(id+"F12.wireOp",EDGE,"E74.1");var subQ18=sQuery(id+"F12.wireOp",EDGE,"E74.8");Q0=qUnion([makeQuery(id+"F12.imprint","IMPRINT",FACE,{"disambiguationData":[TD([[makeQuery(id+"F12.imprint","IMPRINT",EDGE,{"derivedFrom":subQ7}),1.0]])]}),makeQuery(id+"F12.imprint","IMPRINT",FACE,{"disambiguationData":[TD([[makeQuery(id+"F12.imprint","IMPRINT",EDGE,{"derivedFrom":subQ14}),1.0]])]}),makeQuery(id+"F12.imprint","IMPRINT",FACE,{"disambiguationData":[TD([[makeQuery(id+"F12.imprint","IMPRINT",EDGE,{"derivedFrom":subQ16}),1.0]])]}),makeQuery(id+"F12.imprint","IMPRINT",FACE,{"disambiguationData":[TD([[makeQuery(id+"F12.imprint","IMPRINT",EDGE,{"derivedFrom":subQ18}),-1.0]])]})]);}
            var Q1;
            Q1=makeQuery(id+"F5.boolean.opBoolean","SPLIT",FACE,{"disambiguationData":[TD([makeQuery(id+"F5.opExtrude","SWEPT_FACE",FACE,{"disambiguationData":[OSD([sQuery(id+"F4.wireOp",EDGE,"E41")])]})])],"derivedFrom":makeQuery(id+"F3.boolean.opBoolean","COPY",FACE,{"derivedFrom":makeQuery(id+"F3.opExtrude","CAP_FACE",FACE,{"disambiguationData":[OSD([sQuery(id+"F0.wireOp",EDGE,"E25.0"),sQuery(id+"F0.wireOp",EDGE,"E25.1"),sQuery(id+"F0.wireOp",EDGE,"E25.2"),sQuery(id+"F0.wireOp",EDGE,"E25.3"),sQuery(id+"F0.wireOp",EDGE,"E25.4"),sQuery(id+"F0.wireOp",EDGE,"E25.5"),sQuery(id+"F0.wireOp",EDGE,"E25.6"),sQuery(id+"F0.wireOp",EDGE,"E25.7")])],"isStart":false})})});
            extrude(context, id + "F13", {"entities" : qUnion([Q0]), "operationType" : NewBodyOperationType.REMOVE, "endBound" : BoundingType.UP_TO_SURFACE, "endBoundEntityFace" : qUnion([Q1]), "depth" : 25 * mm});
        }
        {
            var Q0;
            Q0=makeQuery(id+"F3.boolean.opBoolean","COPY",EDGE,{"derivedFrom":makeQuery(id+"F3.opExtrude","CAP_EDGE",EDGE,{"disambiguationData":[OSD([sQuery(id+"F0.wireOp",EDGE,"E25.6")])],"isStart":false})});
            var Q1;
            Q1=makeQuery(id+"F8.boolean.opBoolean","INTERSECT",EDGE,{"derivedFrom":[makeQuery(id+"F5.opExtrude","SWEPT_FACE",FACE,{"disambiguationData":[OSD([sQuery(id+"F4.wireOp",EDGE,"E30")])]}),makeQuery(id+"F8.opExtrude","CAP_FACE",FACE,{"disambiguationData":[OSD([sQuery(id+"F7.wireOp",EDGE,"E67")])],"isStart":false})]});
            var Q2;
            Q2=makeQuery(id+"F8.boolean.opBoolean","INTERSECT",EDGE,{"disambiguationData":[OD(1.0)],"derivedFrom":[makeQuery(id+"F5.opExtrude","SWEPT_FACE",FACE,{"disambiguationData":[OSD([sQuery(id+"F4.wireOp",EDGE,"E30")])]}),makeQuery(id+"F8.opExtrude","SWEPT_FACE",FACE,{"disambiguationData":[OSD([sQuery(id+"F7.wireOp",EDGE,"E67")])]})]});
            var Q3;
            {var subQ0=makeQuery(id+"F3.boolean.opBoolean","COPY",FACE,{"derivedFrom":makeQuery(id+"F3.opExtrude","CAP_FACE",FACE,{"disambiguationData":[OSD([sQuery(id+"F0.wireOp",EDGE,"E25.0"),sQuery(id+"F0.wireOp",EDGE,"E25.1"),sQuery(id+"F0.wireOp",EDGE,"E25.2"),sQuery(id+"F0.wireOp",EDGE,"E25.3"),sQuery(id+"F0.wireOp",EDGE,"E25.4"),sQuery(id+"F0.wireOp",EDGE,"E25.5"),sQuery(id+"F0.wireOp",EDGE,"E25.6"),sQuery(id+"F0.wireOp",EDGE,"E25.7")])],"isStart":false})});var subQ1=sQuery(id+"F4.wireOp",EDGE,"E30");Q3=makeQuery(id+"F8.boolean.opBoolean","SPLIT",EDGE,{"disambiguationData":[TD([makeQuery(id+"F5.opExtrude","SWEPT_FACE",FACE,{"disambiguationData":[OSD([sQuery(id+"F4.wireOp",EDGE,"E35.filletArc")])]})])],"derivedFrom":makeQuery(id+"F5.opExtrude","TWEAK_EDGE",EDGE,{"derivedFrom":[subQ0,makeQuery(id+"F4.imprint","IMPRINT",EDGE,{"derivedFrom":subQ1})]})});}
            var Q4;
            {var subQ0=sQuery(id+"F0.wireOp",EDGE,"E25.0");var subQ1=sQuery(id+"F0.wireOp",EDGE,"E25.1");var subQ2=sQuery(id+"F0.wireOp",EDGE,"E25.2");var subQ3=sQuery(id+"F0.wireOp",EDGE,"E25.3");var subQ4=sQuery(id+"F0.wireOp",EDGE,"E25.4");var subQ5=sQuery(id+"F0.wireOp",EDGE,"E25.5");var subQ6=sQuery(id+"F0.wireOp",EDGE,"E25.6");var subQ7=sQuery(id+"F0.wireOp",EDGE,"E25.7");Q4=makeQuery(id+"F8.boolean.opBoolean","INTERSECT",EDGE,{"derivedFrom":[makeQuery(id+"F5.boolean.opBoolean","SPLIT",FACE,{"disambiguationData":[TD([makeQuery(id+"F2.opExtrude","SWEPT_FACE",FACE,{"disambiguationData":[OSD([subQ0])]})])],"derivedFrom":makeQuery(id+"F3.boolean.opBoolean","COPY",FACE,{"derivedFrom":makeQuery(id+"F3.opExtrude","CAP_FACE",FACE,{"disambiguationData":[OSD([subQ0,subQ1,subQ2,subQ3,subQ4,subQ5,subQ6,subQ7])],"isStart":false})})}),makeQuery(id+"F8.opExtrude","SWEPT_FACE",FACE,{"disambiguationData":[OSD([sQuery(id+"F7.wireOp",EDGE,"E67")])]})]});}
            var Q5;
            Q5=makeQuery(id+"F8.boolean.opBoolean","INTERSECT",EDGE,{"disambiguationData":[OD(0.0)],"derivedFrom":[makeQuery(id+"F5.opExtrude","SWEPT_FACE",FACE,{"disambiguationData":[OSD([sQuery(id+"F4.wireOp",EDGE,"E30")])]}),makeQuery(id+"F8.opExtrude","SWEPT_FACE",FACE,{"disambiguationData":[OSD([sQuery(id+"F7.wireOp",EDGE,"E67")])]})]});
            fillet(context, id + "F14", {"entities" : qUnion([Q0, Q1, Q2, Q3, Q4, Q5]), "radius" : 3 * mm, "tangentPropagation" : true, "allowEdgeOverflow" : false});
        }
        {
            var Q0;
            Q0=makeQuery(id+"F1.opExtrude","CAP_EDGE",EDGE,{"disambiguationData":[OSD([sQuery(id+"F0.wireOp",EDGE,"E1.bottom")])],"isStart":false});
            fillet(context, id + "F15", {"entities" : qUnion([Q0]), "radius" : 2 * mm, "tangentPropagation" : true, "allowEdgeOverflow" : false});
        }
        {
            var Q0;
            {var subQ0=sQuery(id+"F0.wireOp",EDGE,"E22.filletArc");var subQ1=sQuery(id+"F0.wireOp",EDGE,"E7");var subQ2=sQuery(id+"F0.wireOp",EDGE,"E6");var subQ3=sQuery(id+"F0.wireOp",EDGE,"E5");var subQ4=sQuery(id+"F0.wireOp",EDGE,"E4");var subQ5=sQuery(id+"F0.wireOp",EDGE,"E1.bottom");var subQ6=sQuery(id+"F0.wireOp",EDGE,"E21.filletArc");var subQ7=sQuery(id+"F0.wireOp",EDGE,"E1.top");var subQ8=sQuery(id+"F0.wireOp",EDGE,"E1.left");var subQ9=sQuery(id+"F0.wireOp",EDGE,"E1.right");var subQ10=sQuery(id+"F0.wireOp",EDGE,"E23.filletArc");var subQ11=sQuery(id+"F0.wireOp",EDGE,"E24.filletArc");Q0=makeQuery(id+"F2.boolean.opBoolean","SPLIT",FACE,{"disambiguationData":[TD([makeQuery(id+"F1.opExtrude","SWEPT_FACE",FACE,{"disambiguationData":[OSD([subQ5])]})])],"derivedFrom":makeQuery(id+"F1.opExtrude","CAP_FACE",FACE,{"disambiguationData":[OSD([subQ5,subQ7,subQ8,subQ9,subQ4,subQ3,subQ2,subQ1,subQ6,subQ0,subQ10,subQ11])],"isStart":true})});}
            var sketch = newSketch(context, id + "F16", { "sketchPlane" : qUnion([Q0])});
            skLineSegment(sketch, "E79", {"start": v(0, 80) * mm, "end": v(0, 110) * mm, "construction": true});
            skPoint(sketch, "E79.endSnap0", {"position": v(0, 80) * mm});
            skLineSegment(sketch, "E80", {"start": v(-14.06, 115.23) * mm, "end": v(-14.06, 98) * mm});
            skCircle(sketch, "E81", {"center": v(0, 110) * mm, "radius": 6 * mm});
            skLineSegment(sketch, "E82", {"start": v(-14.06, 98) * mm, "end": v(-32.06, 80) * mm});
            skArc(sketch, "E83", {"start": v(14.06, 115.23) * mm, "mid": v(0, 125) * mm, "end": v(-14.06, 115.23) * mm});
            skLineSegment(sketch, "E84.MirrorCS", {"start": v(14.06, 115.23) * mm, "end": v(14.06, 98) * mm});
            skArc(sketch, "E85.MirrorCS", {"start": v(-14.06, 115.23) * mm, "mid": v(0, 125) * mm, "end": v(14.06, 115.23) * mm});
            skLineSegment(sketch, "E86.MirrorCS", {"start": v(14.06, 98) * mm, "end": v(32.06, 80) * mm});
            skLineSegment(sketch, "E87", {"start": v(-32.06, 80) * mm, "end": v(32.06, 80) * mm});
            skLineSegment(sketch, "E88", {"start": v(-90, 0) * mm, "end": v(90, 0) * mm, "construction": true});
            skCircle(sketch, "E89.MirrorC", {"center": v(0, -110) * mm, "radius": 6 * mm});
            skLineSegment(sketch, "E90.MirrorCS", {"start": v(14.06, -115.23) * mm, "end": v(14.06, -98) * mm});
            skArc(sketch, "E91.MirrorCS", {"start": v(14.06, -115.23) * mm, "mid": v(0, -125) * mm, "end": v(-14.06, -115.23) * mm});
            skLineSegment(sketch, "E92.MirrorCS", {"start": v(-14.06, -115.23) * mm, "end": v(-14.06, -98) * mm});
            skArc(sketch, "E93.MirrorCS", {"start": v(-14.06, -115.23) * mm, "mid": v(0, -125) * mm, "end": v(14.06, -115.23) * mm});
            skLineSegment(sketch, "E94.MirrorCS", {"start": v(0, -80) * mm, "end": v(0, -110) * mm, "construction": true});
            skLineSegment(sketch, "E95.MirrorCS", {"start": v(14.06, -98) * mm, "end": v(32.06, -80) * mm});
            skLineSegment(sketch, "E96.MirrorCS", {"start": v(-14.06, -98) * mm, "end": v(-32.06, -80) * mm});
            skSolve(sketch);
        }
        {
            var Q0;
            Q0=makeQuery(id+"F16.imprint","IMPRINT",FACE,{"disambiguationData":[TD([[makeQuery(id+"F16.imprint","IMPRINT",EDGE,{"derivedFrom":sQuery(id+"F16.wireOp",EDGE,"E80")}),1.0]])]});
            var Q1;
            Q1=makeQuery(id+"F16.imprint","IMPRINT",FACE,{"disambiguationData":[TD([[makeQuery(id+"F16.imprint","IMPRINT",EDGE,{"derivedFrom":sQuery(id+"F16.wireOp",EDGE,"E89.MirrorC")}),-1.0]])]});
            var Q2;
            {var subQ27=sQuery(id+"F16.wireOp",EDGE,"E87");Q2=makeQuery(id+"F16.imprint","IMPRINT",FACE,{"disambiguationData":[TD([[makeQuery(id+"F16.imprint","IMPRINT",EDGE,{"derivedFrom":subQ27}),-1.0]])]});}
            extrude(context, id + "F17", {"entities" : qUnion([Q0, Q1, Q2]), "endBound" : BoundingType.SYMMETRIC, "depth" : 6 * mm});
        }
    });
